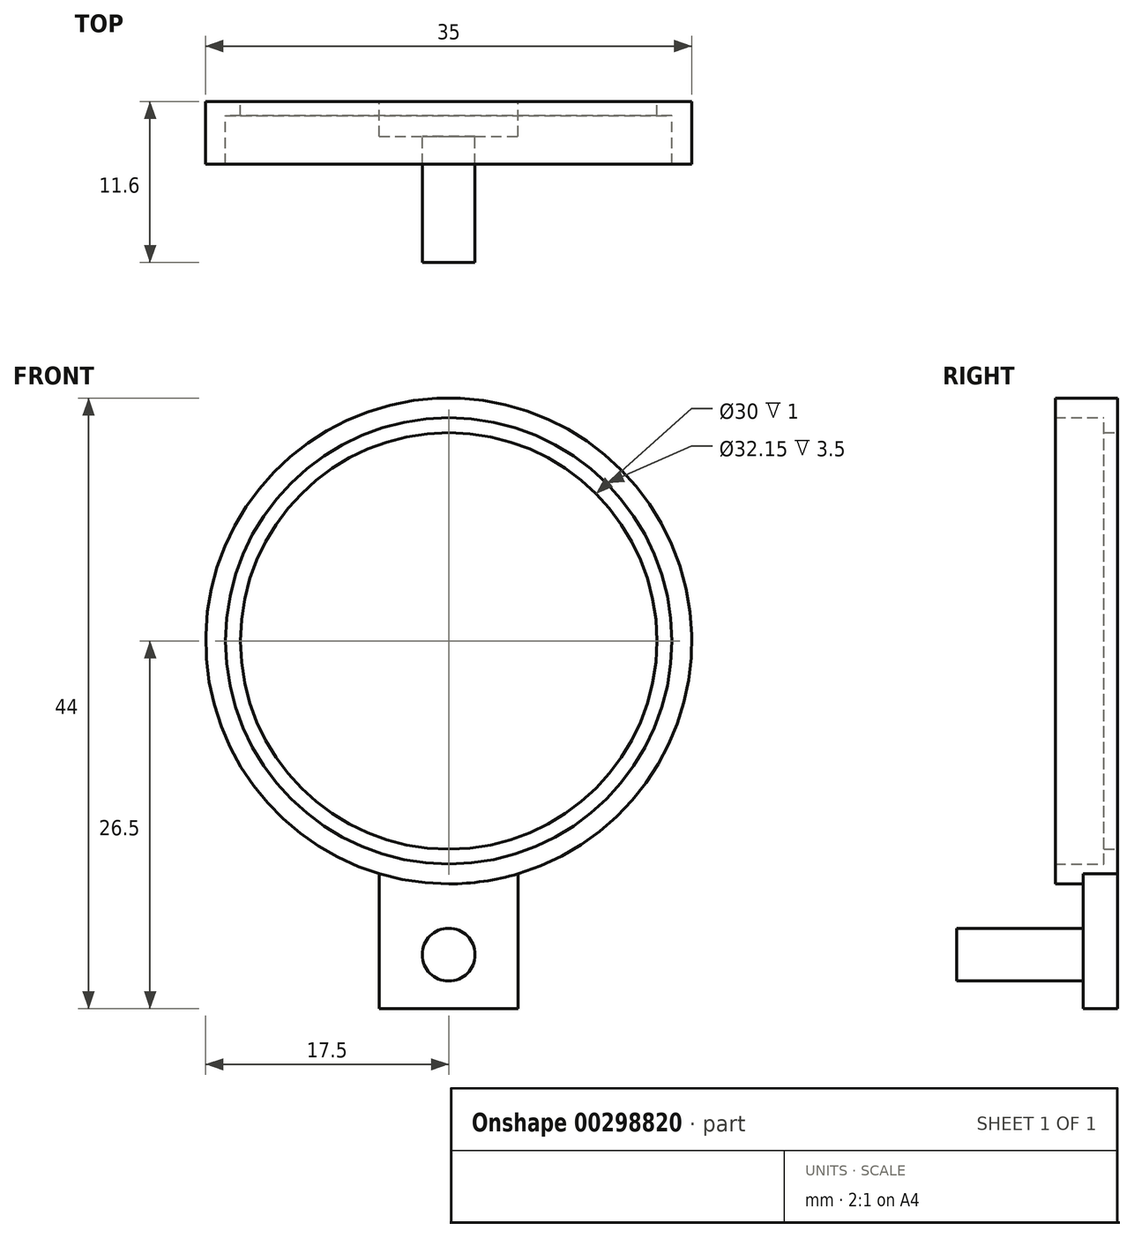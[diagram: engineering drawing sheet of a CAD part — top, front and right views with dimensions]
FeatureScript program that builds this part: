
annotation { "Feature Type Name" : "Feature", "Feature Type Description" : "" }
export const myFeature = defineFeature(function(context is Context, id is Id, definition is map)
    precondition{}
    {
        {
            var Q0;
            Q0=qCreatedBy(makeId("Front.planeOp"),FACE);
            var sketch = newSketch(context, id + "F0", { "sketchPlane" : qUnion([Q0])});
            skCircle(sketch, "E0", {"center": v(0, 0) * mm, "radius": 15 * mm});
            skArc(sketch, "E1", {"start": v(5, -16.77) * mm, "mid": v(0, 17.5) * mm, "end": v(-5, -16.77) * mm});
            skLineSegment(sketch, "E2", {"start": v(-5, -16.77) * mm, "end": v(-5, -26.5) * mm});
            skLineSegment(sketch, "E3", {"start": v(-5, -26.5) * mm, "end": v(5, -26.5) * mm});
            skLineSegment(sketch, "E4", {"start": v(5, -26.5) * mm, "end": v(5, -16.77) * mm});
            skSolve(sketch);
        }
        {
            var Q0;
            Q0=makeQuery(id+"F0.imprint","IMPRINT",FACE,{"disambiguationData":[TD([[makeQuery(id+"F0.imprint","IMPRINT",EDGE,{"derivedFrom":sQuery(id+"F0.wireOp",EDGE,"E0")}),-1.0]])]});
            extrude(context, id + "F1", {"entities" : qUnion([Q0]), "depth" : 1 * mm});
        }
        {
            var Q0;
            Q0=makeQuery(id+"F1.opExtrude","CAP_FACE",FACE,{"disambiguationData":[OSD([sQuery(id+"F0.wireOp",EDGE,"E0"),sQuery(id+"F0.wireOp",EDGE,"E1"),sQuery(id+"F0.wireOp",EDGE,"E2"),sQuery(id+"F0.wireOp",EDGE,"E3"),sQuery(id+"F0.wireOp",EDGE,"E4")])],"isStart":false});
            var sketch = newSketch(context, id + "F2", { "sketchPlane" : qUnion([Q0])});
            skCircle(sketch, "E5", {"center": v(0, 0) * mm, "radius": 16.07 * mm});
            skCircle(sketch, "E6", {"center": v(0, 0) * mm, "radius": 17.5 * mm});
            skSolve(sketch);
        }
        {
            var Q0;
            Q0=makeQuery(id+"F2.imprint","IMPRINT",FACE,{"disambiguationData":[TD([[makeQuery(id+"F2.imprint","IMPRINT",EDGE,{"derivedFrom":sQuery(id+"F2.wireOp",EDGE,"E5")}),-1.0]])]});
            extrude(context, id + "F3", {"entities" : qUnion([Q0]), "operationType" : NewBodyOperationType.ADD, "depth" : 3.5 * mm});
        }
        {
            var Q0;
            {var subQ0=sQuery(id+"F0.wireOp",EDGE,"E4");var subQ1=sQuery(id+"F0.wireOp",EDGE,"E3");var subQ2=sQuery(id+"F0.wireOp",EDGE,"E2");var subQ3=sQuery(id+"F0.wireOp",EDGE,"E1");Q0=makeQuery(id+"F3.boolean.opBoolean","SPLIT",FACE,{"disambiguationData":[TD([makeQuery(id+"F1.opExtrude","SWEPT_FACE",FACE,{"disambiguationData":[OSD([subQ3])]})])],"derivedFrom":makeQuery(id+"F1.opExtrude","CAP_FACE",FACE,{"disambiguationData":[OSD([sQuery(id+"F0.wireOp",EDGE,"E0"),subQ3,subQ2,subQ1,subQ0])],"isStart":false})});}
            extrude(context, id + "F4", {"entities" : qUnion([Q0]), "operationType" : NewBodyOperationType.ADD, "depth" : 1.5 * mm});
        }
        {
            var Q0;
            Q0=makeQuery(id+"F4.opExtrude","CAP_FACE",FACE,{"disambiguationData":[OSD([sQuery(id+"F0.wireOp",EDGE,"E0"),sQuery(id+"F0.wireOp",EDGE,"E1"),sQuery(id+"F0.wireOp",EDGE,"E2"),sQuery(id+"F0.wireOp",EDGE,"E3"),sQuery(id+"F0.wireOp",EDGE,"E4")])],"isStart":false});
            var sketch = newSketch(context, id + "F5", { "sketchPlane" : qUnion([Q0])});
            skCircle(sketch, "E7", {"center": v(0, -22.6) * mm, "radius": 1.9 * mm});
            skSolve(sketch);
        }
        {
            var Q0;
            Q0=makeQuery(id+"F5.imprint","IMPRINT",FACE,{"disambiguationData":[TD([[makeQuery(id+"F5.imprint","IMPRINT",EDGE,{"derivedFrom":sQuery(id+"F5.wireOp",EDGE,"E7")}),1.0]])]});
            var Q1;
            Q1=makeQuery(id+"F3.opExtrude","CAP_FACE",FACE,{"disambiguationData":[OSD([sQuery(id+"F2.wireOp",EDGE,"E5"),sQuery(id+"F2.wireOp",EDGE,"E6")])],"isStart":false});
            extrude(context, id + "F6", {"entities" : qUnion([Q0]), "operationType" : NewBodyOperationType.ADD, "endBoundEntityFace" : qUnion([Q1]), "depth" : 9.1 * mm});
        }
    });
